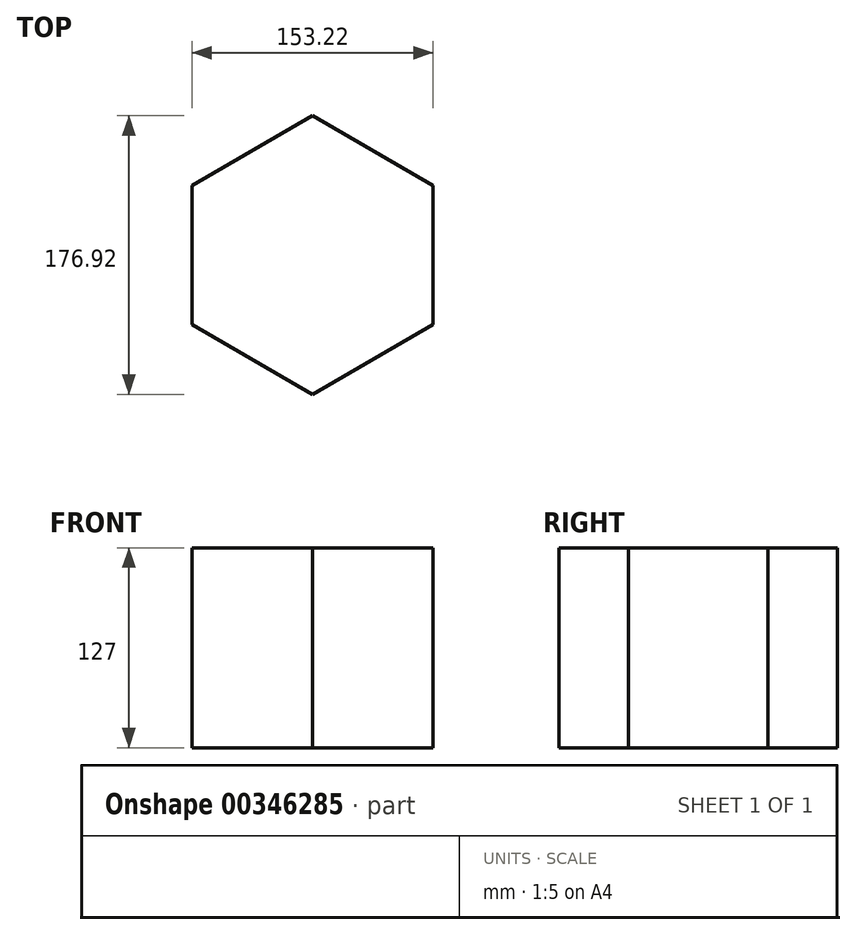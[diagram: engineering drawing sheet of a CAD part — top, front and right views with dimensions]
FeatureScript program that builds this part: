
annotation { "Feature Type Name" : "Feature", "Feature Type Description" : "" }
export const myFeature = defineFeature(function(context is Context, id is Id, definition is map)
    precondition{}
    {
        {
            var Q0;
            Q0=qCreatedBy(makeId("Top.planeOp"),FACE);
            var sketch = newSketch(context, id + "F0", { "sketchPlane" : qUnion([Q0])});
            skCircle(sketch, "E0.cCircle", {"center": v(0, 0) * mm, "radius": 76.61 * mm, "construction": true});
            skLineSegment(sketch, "E0.0", {"start": v(-76.61, -44.23) * mm, "end": v(-76.61, 44.23) * mm});
            skLineSegment(sketch, "E0.1", {"start": v(-76.61, 44.23) * mm, "end": v(0, 88.46) * mm});
            skLineSegment(sketch, "E0.2", {"start": v(0, 88.46) * mm, "end": v(76.61, 44.23) * mm});
            skLineSegment(sketch, "E0.3", {"start": v(76.61, 44.23) * mm, "end": v(76.61, -44.23) * mm});
            skLineSegment(sketch, "E0.4", {"start": v(76.61, -44.23) * mm, "end": v(0, -88.46) * mm});
            skLineSegment(sketch, "E0.5", {"start": v(0, -88.46) * mm, "end": v(-76.61, -44.23) * mm});
            skPoint(sketch, "E0.0.midPoint", {"position": v(-76.61, 0) * mm});
            skSolve(sketch);
        }
        {
            var Q0;
            Q0 = qSketchRegion(id + "F0", true);
            extrude(context, id + "F1", {"entities" : qUnion([Q0]), "depth" : 127 * mm});
        }
    });
